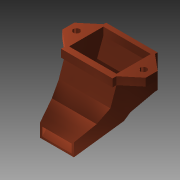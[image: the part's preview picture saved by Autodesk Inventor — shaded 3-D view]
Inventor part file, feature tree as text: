
AUTODESK INVENTOR PART (.ipt)
format: ipt  version: 2013 (Build 170138000, 138)  size: 157,696 bytes
history: native  units: mm
features: extrude x5, sketch x5, shell x1
ambient origin geometry x8: Origin, YZ Plane, XZ Plane, XY Plane, X Axis, Y Axis, Z Axis, Center Point
bodies: Solid1 (feature_tree)
feature tree (11):
  extrude  "Extrusion1"  Depth=20.0mm TaperAngle=0.0deg
  extrude  "Extrusion2"  Depth=0.8mm
  shell  "Shell1"  Thickness=2.5mm
  extrude  "Extrusion3"  Depth=3.0mm
  extrude  "Extrusion4"  Depth=7.5mm
  extrude  "Extrusion5"  Depth=3.0mm TaperAngle=0.0deg
  sketch  "Sketch1"  dims[d0=15.0mm d1=20.0mm d2=0.0mm]
  sketch  "Sketch2"  dims[d3=25.0mm d4=0.0mm d5=0.8mm d6=2.5mm]
  sketch  "Sketch3"  dims[d8=2.5mm d9=3.0mm]
  sketch  "Sketch4"  dims[d10=3.0mm d11=7.5mm]
  sketch  "Sketch5"  dims[d12=7.5mm d13=3.0mm d14=0.0mm d15=20.0mm d16=0.0mm d17=22.68928mm d18=22.68928mm d19=22.68928mm d20=22.68928mm d21=6.2mm d22=6.2mm d23=1.5mm d24=16.0mm d25=1.0mm d26=0.0mm d27=5.0mm]
